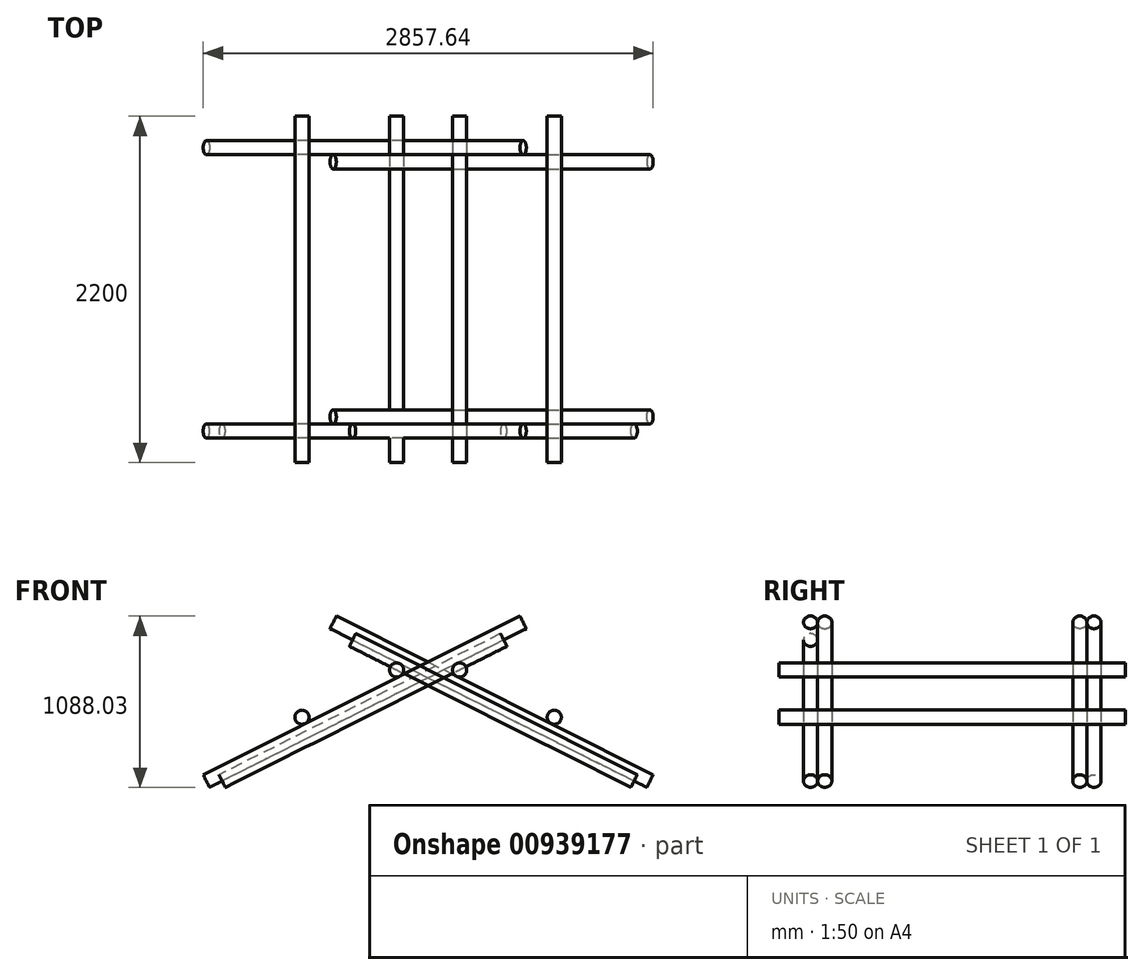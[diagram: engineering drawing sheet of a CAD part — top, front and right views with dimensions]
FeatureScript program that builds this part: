
annotation { "Feature Type Name" : "Feature", "Feature Type Description" : "" }
export const myFeature = defineFeature(function(context is Context, id is Id, definition is map)
    precondition{}
    {
        {
            var Q0;
            Q0=qCreatedBy(makeId("Front.planeOp"),FACE);
            var sketch = newSketch(context, id + "F0", { "sketchPlane" : qUnion([Q0])});
            skCircle(sketch, "E0", {"center": v(-200, 705) * mm, "radius": 45 * mm});
            skCircle(sketch, "E1", {"center": v(200, 705) * mm, "radius": 45 * mm});
            skCircle(sketch, "E2", {"center": v(600, 405) * mm, "radius": 45 * mm});
            skCircle(sketch, "E3", {"center": v(-600, 405) * mm, "radius": 45 * mm});
            skLineSegment(sketch, "E4", {"start": v(-300, 750) * mm, "end": v(300, 750) * mm});
            skLineSegment(sketch, "E5", {"start": v(-300, 660) * mm, "end": v(300, 660) * mm});
            skLineSegment(sketch, "E6", {"start": v(300, 750) * mm, "end": v(300, 660) * mm});
            skLineSegment(sketch, "E7", {"start": v(-300, 750) * mm, "end": v(-300, 660) * mm});
            skSolve(sketch);
        }
        {
            var Q0;
            Q0=qCreatedBy(makeId("Front.planeOp"),FACE);
            var sketch = newSketch(context, id + "F1", { "sketchPlane" : qUnion([Q0])});
            skCircle(sketch, "E8.0", {"center": v(-200, 705) * mm, "radius": 45 * mm});
            skCircle(sketch, "E9.0", {"center": v(-600, 405) * mm, "radius": 45 * mm});
            skCircle(sketch, "E10.0", {"center": v(200, 705) * mm, "radius": 45 * mm});
            skCircle(sketch, "E11.0", {"center": v(600, 405) * mm, "radius": 45 * mm});
            skLineSegment(sketch, "E12", {"start": v(-1308.18, 0) * mm, "end": v(559.05, 935.15) * mm});
            skLineSegment(sketch, "E13.MirrorCS", {"start": v(1308.18, 0) * mm, "end": v(-559.05, 935.15) * mm});
            skSolve(sketch);
        }
        {
            var Q0;
            Q0=sQuery(id+"F1.wireOp",EDGE,"E12");
            var Q1;
            Q1=sQuery(id+"F1.wireOp",VERTEX,"E12.start");
            cPlane(context, id + "F2", {"entities" : qUnion([Q0, Q1]), "cplaneType" : CPlaneType.LINE_POINT, "offset" : 25 * mm, "width" : 150 * mm, "height" : 150 * mm});
        }
        {
            var Q0;
            Q0=qCreatedBy(id+"F2.planeOp",FACE);
            var sketch = newSketch(context, id + "F3", { "sketchPlane" : qUnion([Q0])});
            skPoint(sketch, "E14.0", {"position": v(0, 585.8) * mm});
            skCircle(sketch, "E15", {"center": v(0, 585.8) * mm, "radius": 45 * mm});
            skSolve(sketch);
        }
        {
            var Q0;
            Q0=makeQuery(id+"F3.imprint","IMPRINT",FACE,{"disambiguationData":[TD([[makeQuery(id+"F3.imprint","IMPRINT",EDGE,{"derivedFrom":sQuery(id+"F3.wireOp",EDGE,"E15")}),1.0]])]});
            extrude(context, id + "F4", {"entities" : qUnion([Q0]), "depth" : 2000 * mm, "offsetDistance" : 25 * mm});
        }
        {
            var Q0;
            Q0=makeQuery(id+"F4.opExtrude","SWEPT_BODY",BODY,{"disambiguationData":[OSD([sQuery(id+"F3.wireOp",EDGE,"E15")])]});
            var Q1;
            Q1=qCreatedBy(makeId("Right.planeOp"),FACE);
            mirror(context, id + "F5", {"entities" : qUnion([Q0]), "mirrorPlane" : qUnion([Q1])});
        }
        {
            var Q0;
            Q0=qCreatedBy(makeId("Front.planeOp"),FACE);
            var sketch = newSketch(context, id + "F6", { "sketchPlane" : qUnion([Q0])});
            skCircle(sketch, "E16.0", {"center": v(-600, 405) * mm, "radius": 45 * mm});
            skCircle(sketch, "E17.0", {"center": v(200, 705) * mm, "radius": 45 * mm});
            skLineSegment(sketch, "E18", {"start": v(-1308.18, 0) * mm, "end": v(825.24, 1068.46) * mm});
            skLineSegment(sketch, "E19", {"start": v(-1408.67, 0) * mm, "end": v(966.75, 1189.66) * mm});
            skSolve(sketch);
        }
        {
            var Q0;
            Q0=sQuery(id+"F6.wireOp",VERTEX,"E19.start");
            var Q1;
            Q1=sQuery(id+"F6.wireOp",EDGE,"E19");
            cPlane(context, id + "F7", {"entities" : qUnion([Q0, Q1]), "cplaneType" : CPlaneType.LINE_POINT, "offset" : 25 * mm, "width" : 150 * mm, "height" : 150 * mm});
        }
        {
            var Q0;
            Q0=qCreatedBy(id+"F7.planeOp",FACE);
            var sketch = newSketch(context, id + "F8", { "sketchPlane" : qUnion([Q0])});
            skPoint(sketch, "E20.0", {"position": v(0, 630.8) * mm});
            skCircle(sketch, "E21", {"center": v(0, 630.8) * mm, "radius": 45 * mm});
            skSolve(sketch);
        }
        {
            var Q0;
            Q0=makeQuery(id+"F8.imprint","IMPRINT",FACE,{"disambiguationData":[TD([[makeQuery(id+"F8.imprint","IMPRINT",EDGE,{"derivedFrom":sQuery(id+"F8.wireOp",EDGE,"E21")}),1.0]])]});
            extrude(context, id + "F9", {"entities" : qUnion([Q0]), "depth" : 2250 * mm, "offsetDistance" : 25 * mm});
        }
        {
            var Q0;
            Q0=makeQuery(id+"F9.opExtrude","SWEPT_BODY",BODY,{"disambiguationData":[OSD([sQuery(id+"F8.wireOp",EDGE,"E21")])]});
            var Q1;
            Q1=qCreatedBy(makeId("Right.planeOp"),FACE);
            mirror(context, id + "F10", {"entities" : qUnion([Q0]), "mirrorPlane" : qUnion([Q1])});
        }
        {
            var Q0;
            Q0=qCreatedBy(makeId("Front.planeOp"),FACE);
            var sketch = newSketch(context, id + "F11", { "sketchPlane" : qUnion([Q0])});
            skPoint(sketch, "E22.0", {"position": v(-600, 405) * mm});
            skLineSegment(sketch, "E23", {"start": v(-1086.14, 405) * mm, "end": v(1293.67, 405) * mm, "construction": true});
            skLineSegment(sketch, "E24", {"start": v(-1428.82, 40.24) * mm, "end": v(582.98, 1047.79) * mm, "construction": true});
            skLineSegment(sketch, "E25", {"start": v(-582.98, 1047.79) * mm, "end": v(1428.82, 40.24) * mm, "construction": true});
            skCircle(sketch, "E26", {"center": v(-800.98, 405) * mm, "radius": 45 * mm});
            skCircle(sketch, "E27.0", {"center": v(-200, 705) * mm, "radius": 45 * mm});
            skLineSegment(sketch, "E28", {"start": v(-200, 750) * mm, "end": v(-500.98, 750) * mm});
            skLineSegment(sketch, "E29", {"start": v(0, 0) * mm, "end": v(0, 1183.45) * mm, "construction": true});
            skLineSegment(sketch, "E30", {"start": v(-200, 750) * mm, "end": v(0, 750) * mm});
            skSolve(sketch);
        }
        {
            var Q0;
            Q0=makeQuery(id+"F11.imprint","IMPRINT",FACE,{"disambiguationData":[TD([[makeQuery(id+"F11.imprint","IMPRINT",EDGE,{"derivedFrom":sQuery(id+"F11.wireOp",EDGE,"E26")}),1.0]])]});
            var Q1;
            {var subQ0=sQuery(id+"F0.wireOp",EDGE,"E0");var subQ1=makeQuery(id+"F0.imprint","INTERSECT",VERTEX,{"derivedFrom":[subQ0,sQuery(id+"F0.wireOp",EDGE,"E4")]});Q1=makeQuery(id+"F0.imprint","IMPRINT",FACE,{"disambiguationData":[TD([[makeQuery(id+"F0.imprint","IMPRINT",EDGE,{"disambiguationData":[TD([[subQ1,-1.0]])],"derivedFrom":subQ0}),1.0]])]});}
            extrude(context, id + "F12", {"entities" : qUnion([Q0, Q1]), "oppositeDirection" : true, "depth" : 2000 * mm, "offsetDistance" : 25 * mm, "hasSecondDirection" : true, "secondDirectionOppositeDirection" : false, "secondDirectionDepth" : 200 * mm});
        }
        {
            var Q0;
            Q0=makeQuery(id+"F10.opPattern","COPY",BODY,{"derivedFrom":makeQuery(id+"F9.opExtrude","SWEPT_BODY",BODY,{"disambiguationData":[OSD([sQuery(id+"F8.wireOp",EDGE,"E21")])]}),"instanceName":"1"});
            transform(context, id + "F13", {"entities" : qUnion([Q0]), "transformType" : TransformType.TRANSLATION_3D, "dx" : 0 * mm, "dy" : 90 * mm, "dz" : 0 * mm, "makeCopy" : false});
        }
        {
            var Q0;
            Q0=makeQuery(id+"F12.opExtrude","SWEPT_BODY",BODY,{"disambiguationData":[OSD([sQuery(id+"F11.wireOp",EDGE,"E26")])]});
            var Q1;
            Q1=makeQuery(id+"F12.opExtrude","SWEPT_BODY",BODY,{"disambiguationData":[OSD([sQuery(id+"F0.wireOp",EDGE,"E0")])]});
            var Q2;
            Q2=qCreatedBy(makeId("Right.planeOp"),FACE);
            mirror(context, id + "F14", {"entities" : qUnion([Q0, Q1]), "mirrorPlane" : qUnion([Q2])});
        }
        {
            var Q0;
            Q0=qCreatedBy(makeId("Top.planeOp"),FACE);
            var sketch = newSketch(context, id + "F15", { "sketchPlane" : qUnion([Q0])});
            skLineSegment(sketch, "E31", {"start": v(845.98, 2000) * mm, "end": v(845.98, -200) * mm});
            skPoint(sketch, "E32", {"position": v(845.98, 900) * mm});
            skSolve(sketch);
        }
        {
            var Q0;
            Q0=sQuery(id+"F15.wireOp",VERTEX,"E32");
            var Q1;
            Q1=sQuery(id+"F15.wireOp",EDGE,"E31");
            cPlane(context, id + "F16", {"entities" : qUnion([Q0, Q1]), "cplaneType" : CPlaneType.LINE_POINT, "offset" : 25 * mm, "width" : 150 * mm, "height" : 150 * mm});
        }
        {
            var Q0;
            Q0=makeQuery(id+"F9.opExtrude","SWEPT_BODY",BODY,{"disambiguationData":[OSD([sQuery(id+"F8.wireOp",EDGE,"E21")])]});
            var Q1;
            Q1=makeQuery(id+"F10.opPattern","COPY",BODY,{"derivedFrom":makeQuery(id+"F9.opExtrude","SWEPT_BODY",BODY,{"disambiguationData":[OSD([sQuery(id+"F8.wireOp",EDGE,"E21")])]}),"instanceName":"1"});
            var Q2;
            Q2=qCreatedBy(id+"F16.planeOp",FACE);
            mirror(context, id + "F17", {"entities" : qUnion([Q0, Q1]), "mirrorPlane" : qUnion([Q2])});
        }
    });
